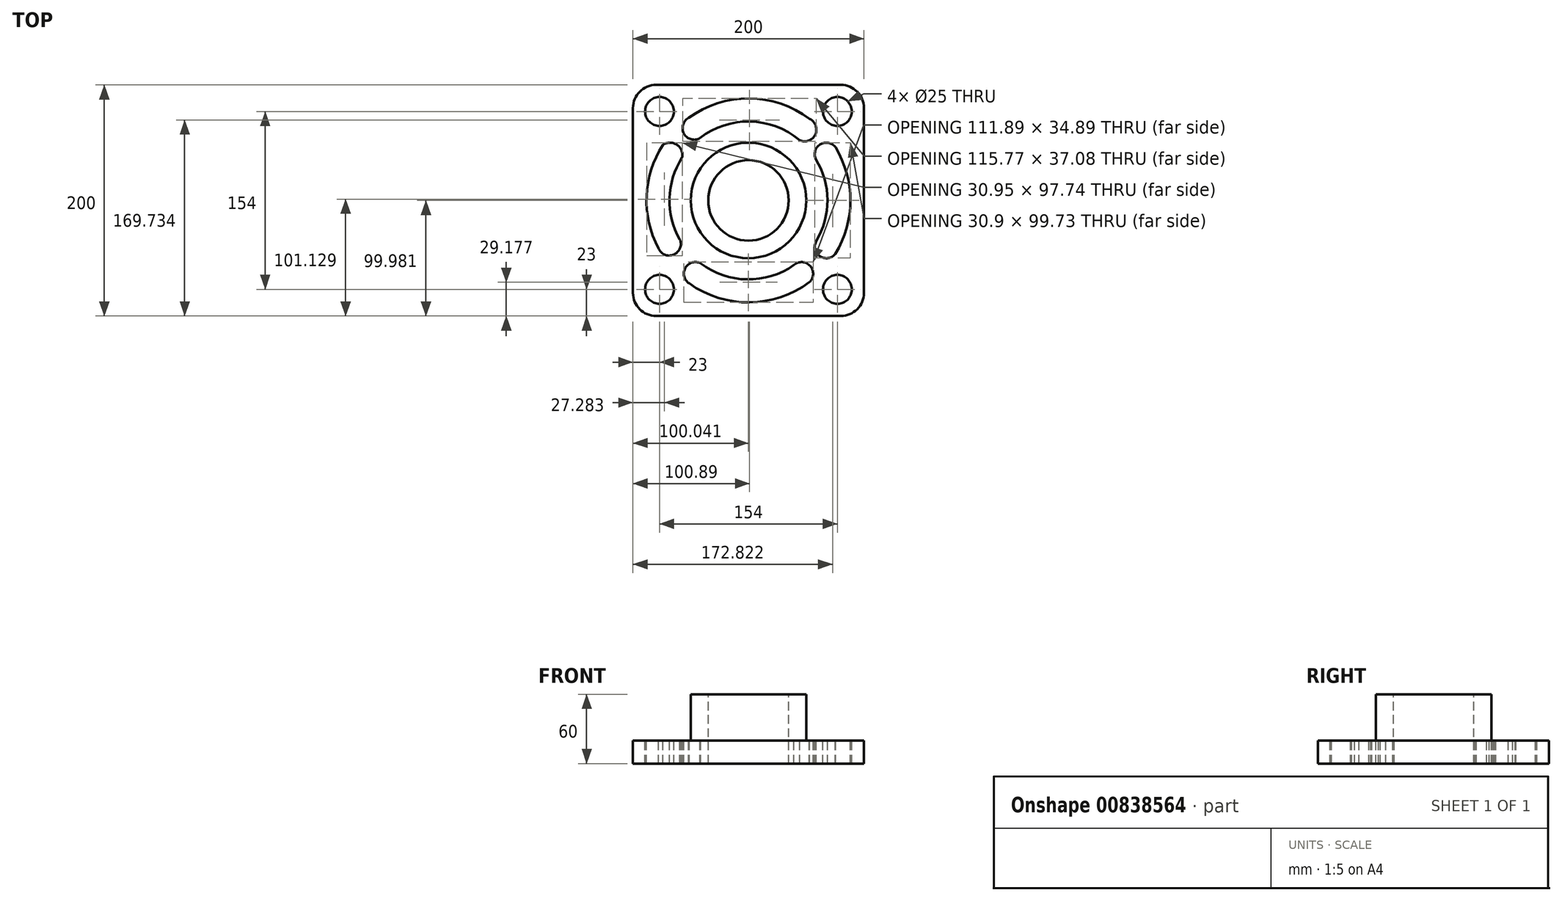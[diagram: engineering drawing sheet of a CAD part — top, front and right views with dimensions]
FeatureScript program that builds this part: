
annotation { "Feature Type Name" : "Feature", "Feature Type Description" : "" }
export const myFeature = defineFeature(function(context is Context, id is Id, definition is map)
    precondition{}
    {
        {
            var Q0;
            Q0=qCreatedBy(makeId("Top.planeOp"),FACE);
            var sketch = newSketch(context, id + "F0", { "sketchPlane" : qUnion([Q0])});
            skLineSegment(sketch, "E0.bottom", {"start": v(80, 100) * mm, "end": v(-80, 100) * mm});
            skLineSegment(sketch, "E0.top", {"start": v(80, -100) * mm, "end": v(-80, -100) * mm});
            skLineSegment(sketch, "E0.left", {"start": v(100, 80) * mm, "end": v(100, -80) * mm});
            skLineSegment(sketch, "E0.right", {"start": v(-100, 80) * mm, "end": v(-100, -80) * mm});
            skPoint(sketch, "E0.middle", {"position": v(0, 0) * mm});
            skPoint(sketch, "E1.visualSharp", {"position": v(-100, 100) * mm});
            skArc(sketch, "E1.filletArc", {"start": v(-80, 100) * mm, "mid": v(-94.14, 94.14) * mm, "end": v(-100, 80) * mm});
            skPoint(sketch, "E2.visualSharp", {"position": v(100, 100) * mm});
            skArc(sketch, "E2.filletArc", {"start": v(100, 80) * mm, "mid": v(94.14, 94.14) * mm, "end": v(80, 100) * mm});
            skPoint(sketch, "E3.visualSharp", {"position": v(100, -100) * mm});
            skArc(sketch, "E3.filletArc", {"start": v(80, -100) * mm, "mid": v(94.14, -94.14) * mm, "end": v(100, -80) * mm});
            skPoint(sketch, "E4.visualSharp", {"position": v(-100, -100) * mm});
            skArc(sketch, "E4.filletArc", {"start": v(-100, -80) * mm, "mid": v(-94.14, -94.14) * mm, "end": v(-80, -100) * mm});
            skCircle(sketch, "E5", {"center": v(-77, 77) * mm, "radius": 12.5 * mm});
            skCircle(sketch, "E6", {"center": v(77, 77) * mm, "radius": 12.5 * mm});
            skCircle(sketch, "E7", {"center": v(-77, -77) * mm, "radius": 12.5 * mm});
            skCircle(sketch, "E8", {"center": v(77, -77) * mm, "radius": 12.5 * mm});
            skSolve(sketch);
        }
        {
            var Q0;
            Q0 = qSketchRegion(id + "F0", true);
            extrude(context, id + "F1", {"entities" : qUnion([Q0]), "oppositeDirection" : true, "depth" : 20 * mm, "offsetDistance" : 25 * mm});
        }
        {
            var Q0;
            Q0=makeQuery(id+"F1.opExtrude","CAP_FACE",FACE,{"disambiguationData":[OSD([sQuery(id+"F0.wireOp",EDGE,"E0.bottom"),sQuery(id+"F0.wireOp",EDGE,"E0.top"),sQuery(id+"F0.wireOp",EDGE,"E0.left"),sQuery(id+"F0.wireOp",EDGE,"E0.right"),sQuery(id+"F0.wireOp",EDGE,"E1.filletArc"),sQuery(id+"F0.wireOp",EDGE,"E2.filletArc"),sQuery(id+"F0.wireOp",EDGE,"E3.filletArc"),sQuery(id+"F0.wireOp",EDGE,"E4.filletArc"),sQuery(id+"F0.wireOp",EDGE,"E5"),sQuery(id+"F0.wireOp",EDGE,"E6"),sQuery(id+"F0.wireOp",EDGE,"E7"),sQuery(id+"F0.wireOp",EDGE,"E8")])],"isStart":true});
            var sketch = newSketch(context, id + "F2", { "sketchPlane" : qUnion([Q0])});
            skCircle(sketch, "E9", {"center": v(0, 0) * mm, "radius": 50 * mm});
            skSolve(sketch);
        }
        {
            var Q0;
            Q0 = qSketchRegion(id + "F2", true);
            extrude(context, id + "F3", {"entities" : qUnion([Q0]), "operationType" : NewBodyOperationType.ADD, "depth" : 40 * mm, "offsetDistance" : 25 * mm});
        }
        {
            var Q0;
            Q0=makeQuery(id+"F3.opExtrude","CAP_FACE",FACE,{"disambiguationData":[OSD([sQuery(id+"F2.wireOp",EDGE,"E9")])],"isStart":false});
            var sketch = newSketch(context, id + "F4", { "sketchPlane" : qUnion([Q0])});
            skCircle(sketch, "E10", {"center": v(0, 0) * mm, "radius": 34.84 * mm});
            skSolve(sketch);
        }
        {
            var Q0;
            Q0 = qSketchRegion(id + "F4", true);
            extrude(context, id + "F5", {"entities" : qUnion([Q0]), "operationType" : NewBodyOperationType.REMOVE, "oppositeDirection" : true, "depth" : 100 * mm, "offsetDistance" : 25 * mm});
        }
        {
            var Q0;
            Q0=qCreatedBy(makeId("Top.planeOp"),FACE);
            var sketch = newSketch(context, id + "F6", { "sketchPlane" : qUnion([Q0])});
            skArc(sketch, "E11", {"start": v(-57.44, 37.09) * mm, "mid": v(-68.35, 1.8) * mm, "end": v(-59.3, -34.02) * mm});
            skArc(sketch, "E12", {"start": v(-74.07, 48.02) * mm, "mid": v(-88.24, 2.59) * mm, "end": v(-76.75, -43.6) * mm});
            skArc(sketch, "E13", {"start": v(-51.96, 71.36) * mm, "mid": v(-55.77, 57.68) * mm, "end": v(-42.1, 53.87) * mm});
            skArc(sketch, "E14", {"start": v(44.2, 52.17) * mm, "mid": v(57.8, 57.02) * mm, "end": v(52.95, 70.63) * mm});
            skArc(sketch, "E15", {"start": v(-57.44, 37.09) * mm, "mid": v(-62.01, 48.25) * mm, "end": v(-74.07, 48.02) * mm});
            skArc(sketch, "E16", {"start": v(-77.96, -41.4) * mm, "mid": v(-64.94, -47.04) * mm, "end": v(-59.3, -34.02) * mm});
            skArc(sketch, "E17", {"start": v(-41.31, -54.48) * mm, "mid": v(-54.66, -58.34) * mm, "end": v(-51.32, -71.83) * mm});
            skArc(sketch, "E18", {"start": v(52.7, -70.81) * mm, "mid": v(53.47, -56.75) * mm, "end": v(39.42, -55.86) * mm});
            skArc(sketch, "E19", {"start": v(75.34, 46) * mm, "mid": v(62.16, 48.55) * mm, "end": v(58.32, 35.7) * mm});
            skArc(sketch, "E20", {"start": v(58.58, -35.25) * mm, "mid": v(61.85, -48.33) * mm, "end": v(75.18, -46.26) * mm});
            skArc(sketch, "E21.trimOffspring", {"start": v(56.55, 67.78) * mm, "mid": v(1.6, 88.26) * mm, "end": v(-54.05, 69.79) * mm});
            skArc(sketch, "E22.trimOffspring", {"start": v(44.2, 52.17) * mm, "mid": v(1.35, 68.36) * mm, "end": v(-42.1, 53.87) * mm});
            skArc(sketch, "E23.trimOffspring", {"start": v(58.58, -35.25) * mm, "mid": v(68.37, 0.26) * mm, "end": v(58.32, 35.7) * mm});
            skArc(sketch, "E24.trimOffspring", {"start": v(75.18, -46.26) * mm, "mid": v(88.27, -0.16) * mm, "end": v(75.34, 46) * mm});
            skArc(sketch, "E25.trimOffspring", {"start": v(-41.31, -54.48) * mm, "mid": v(-0.27, -68.37) * mm, "end": v(40.88, -54.8) * mm});
            skArc(sketch, "E26.trimOffspring", {"start": v(-52.4, -71.05) * mm, "mid": v(0.2, -88.27) * mm, "end": v(52.7, -70.81) * mm});
            skPoint(sketch, "E27.start.orphan", {"position": v(-88.27, 0) * mm});
            skPoint(sketch, "E28.start.orphan", {"position": v(0, -88.27) * mm});
            skSolve(sketch);
        }
        {
            var Q0;
            Q0 = qSketchRegion(id + "F6", true);
            extrude(context, id + "F7", {"entities" : qUnion([Q0]), "operationType" : NewBodyOperationType.REMOVE, "oppositeDirection" : true, "depth" : 25 * mm, "offsetDistance" : 25 * mm});
        }
    });
